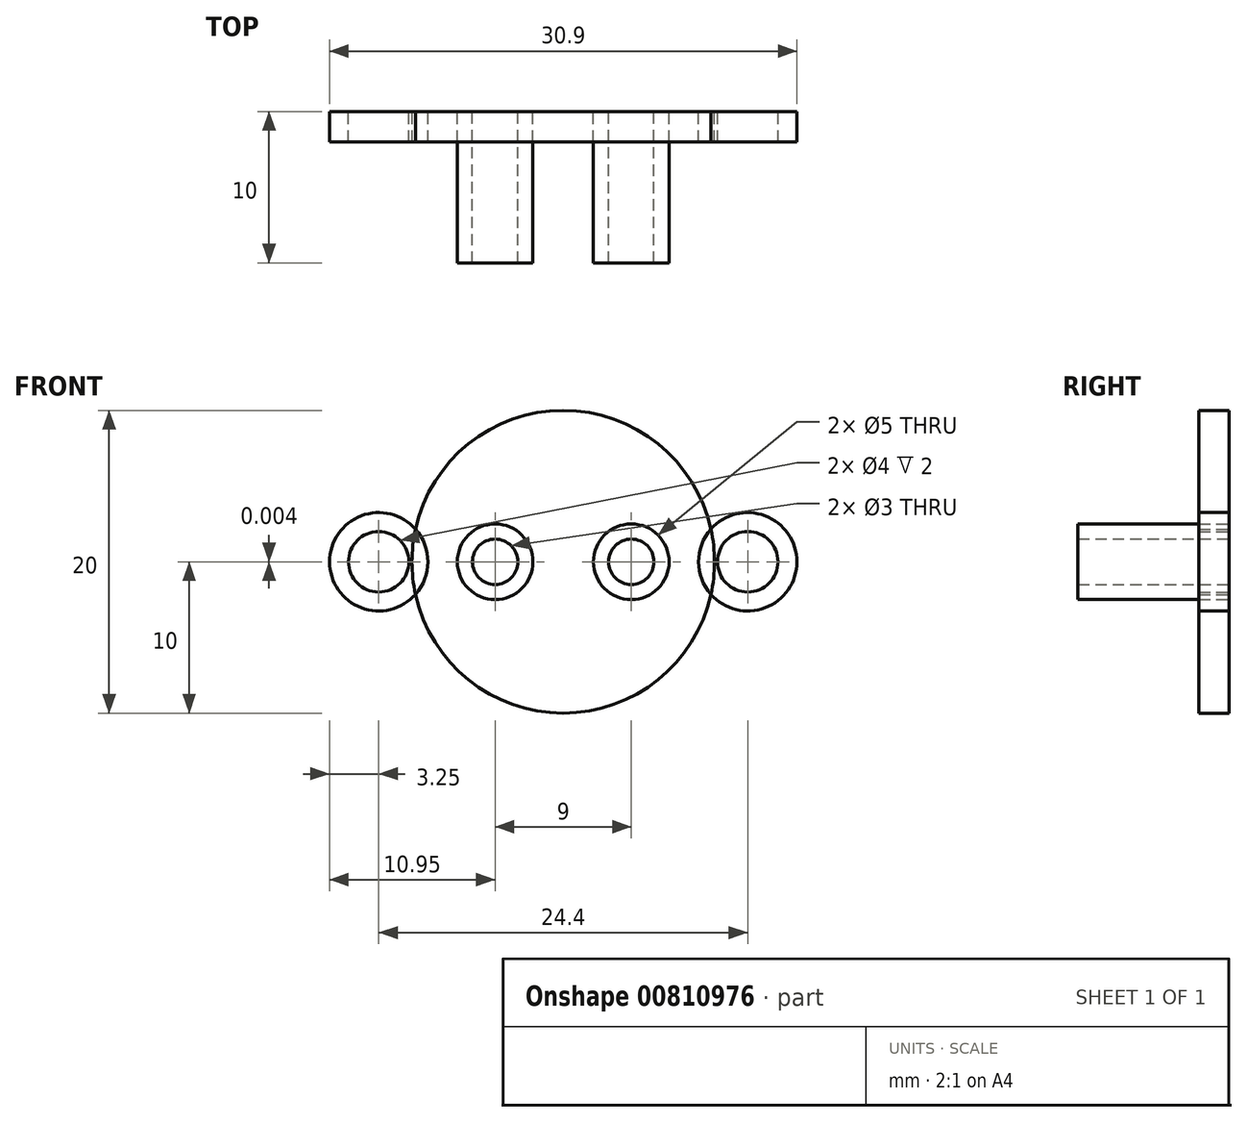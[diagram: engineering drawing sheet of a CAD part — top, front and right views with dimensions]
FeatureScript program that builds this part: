
annotation { "Feature Type Name" : "Feature", "Feature Type Description" : "" }
export const myFeature = defineFeature(function(context is Context, id is Id, definition is map)
    precondition{}
    {
        {
            var Q0;
            Q0=qCreatedBy(makeId("Front.planeOp"),FACE);
            var sketch = newSketch(context, id + "F0", { "sketchPlane" : qUnion([Q0])});
            skCircle(sketch, "E0", {"center": v(0, 0) * mm, "radius": 10 * mm});
            skCircle(sketch, "E1", {"center": v(-4.5, 0) * mm, "radius": 1.5 * mm});
            skCircle(sketch, "E2", {"center": v(4.5, 0) * mm, "radius": 1.5 * mm});
            skCircle(sketch, "E3", {"center": v(-4.5, 0) * mm, "radius": 2.5 * mm});
            skCircle(sketch, "E4", {"center": v(4.5, 0) * mm, "radius": 2.5 * mm});
            skCircle(sketch, "E5", {"center": v(-12.2, 0) * mm, "radius": 3.25 * mm});
            skCircle(sketch, "E6", {"center": v(-12.2, 0) * mm, "radius": 2 * mm});
            skCircle(sketch, "E7", {"center": v(12.2, 0) * mm, "radius": 3.25 * mm});
            skCircle(sketch, "E8", {"center": v(12.2, 0) * mm, "radius": 2 * mm});
            skSolve(sketch);
        }
        {
            var Q0;
            Q0=makeQuery(id+"F0.imprint","IMPRINT",FACE,{"disambiguationData":[TD([[makeQuery(id+"F0.imprint","IMPRINT",EDGE,{"derivedFrom":sQuery(id+"F0.wireOp",EDGE,"E0")}),1.0]])]});
            extrude(context, id + "F1", {"entities" : qUnion([Q0]), "depth" : 2 * mm, "offsetDistance" : 25 * mm});
        }
        {
            var Q0;
            Q0=makeQuery(id+"F0.imprint","IMPRINT",FACE,{"disambiguationData":[TD([[makeQuery(id+"F0.imprint","IMPRINT",EDGE,{"derivedFrom":sQuery(id+"F0.wireOp",EDGE,"E1")}),-1.0]])]});
            var Q1;
            Q1=makeQuery(id+"F0.imprint","IMPRINT",FACE,{"disambiguationData":[TD([[makeQuery(id+"F0.imprint","IMPRINT",EDGE,{"derivedFrom":sQuery(id+"F0.wireOp",EDGE,"E2")}),-1.0]])]});
            extrude(context, id + "F2", {"entities" : qUnion([Q0, Q1]), "operationType" : NewBodyOperationType.ADD, "depth" : 10 * mm, "offsetDistance" : 25 * mm});
        }
        {
            var Q0;
            Q0=makeQuery(id+"F0.imprint","IMPRINT",FACE,{"disambiguationData":[TD([[makeQuery(id+"F0.imprint","IMPRINT",EDGE,{"derivedFrom":sQuery(id+"F0.wireOp",EDGE,"E3")}),-1.0]])]});
            extrude(context, id + "F3", {"entities" : qUnion([Q0]), "depth" : 2 * mm, "offsetDistance" : 25 * mm});
        }
        {
            var Q0;
            {var subQ3=sQuery(id+"F0.wireOp",EDGE,"E8");Q0=makeQuery(id+"F0.imprint","IMPRINT",FACE,{"disambiguationData":[TD([[makeQuery(id+"F0.imprint","IMPRINT",EDGE,{"derivedFrom":subQ3}),-1.0]])]});}
            var Q1;
            {var subQ3=sQuery(id+"F0.wireOp",EDGE,"E6");Q1=makeQuery(id+"F0.imprint","IMPRINT",FACE,{"disambiguationData":[TD([[makeQuery(id+"F0.imprint","IMPRINT",EDGE,{"derivedFrom":subQ3}),-1.0]])]});}
            extrude(context, id + "F4", {"entities" : qUnion([Q0, Q1]), "depth" : 2 * mm, "offsetDistance" : 25 * mm});
        }
        {
            var Q0;
            {var subQ0=sQuery(id+"F0.wireOp",EDGE,"E7");var subQ1=sQuery(id+"F0.wireOp",EDGE,"E0");var subQ2=makeQuery(id+"F0.imprint","INTERSECT",VERTEX,{"disambiguationData":[OD(0.0)],"derivedFrom":[subQ1,subQ0]});Q0=makeQuery(id+"F0.imprint","IMPRINT",FACE,{"disambiguationData":[TD([[makeQuery(id+"F0.imprint","IMPRINT",EDGE,{"disambiguationData":[TD([[subQ2,1.0]])],"derivedFrom":subQ1}),1.0]])]});}
            var Q1;
            {var subQ0=sQuery(id+"F0.wireOp",EDGE,"E5");var subQ1=sQuery(id+"F0.wireOp",EDGE,"E0");var subQ2=makeQuery(id+"F0.imprint","INTERSECT",VERTEX,{"disambiguationData":[OD(0.0)],"derivedFrom":[subQ1,subQ0]});Q1=makeQuery(id+"F0.imprint","IMPRINT",FACE,{"disambiguationData":[TD([[makeQuery(id+"F0.imprint","IMPRINT",EDGE,{"disambiguationData":[TD([[subQ2,-1.0]])],"derivedFrom":subQ1}),1.0]])]});}
            extrude(context, id + "F5", {"entities" : qUnion([Q0, Q1]), "depth" : 2 * mm, "offsetDistance" : 25 * mm});
        }
    });
